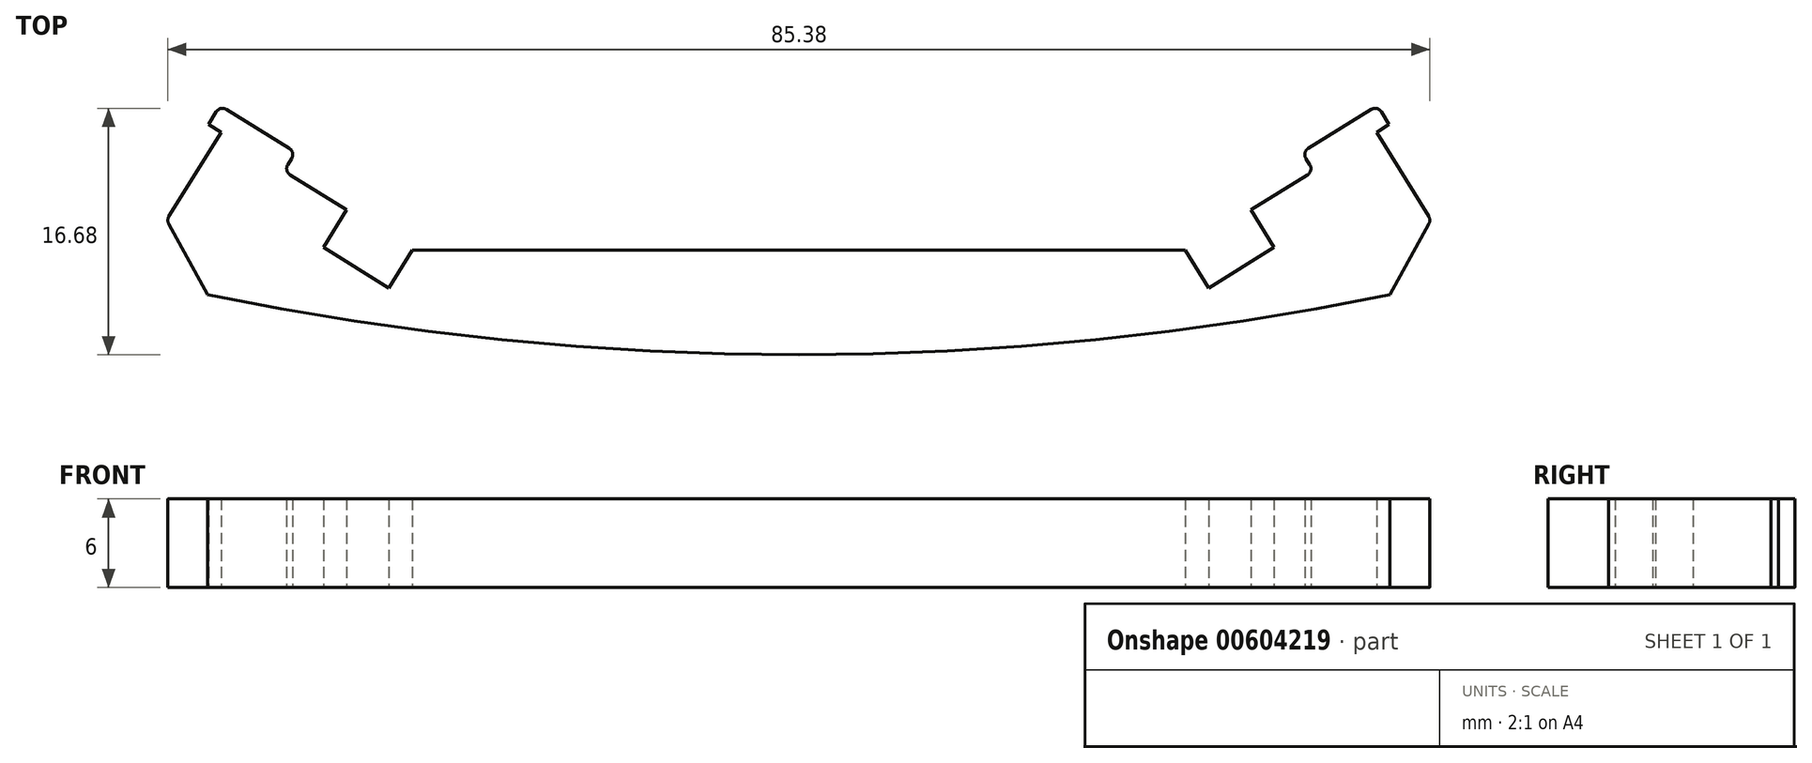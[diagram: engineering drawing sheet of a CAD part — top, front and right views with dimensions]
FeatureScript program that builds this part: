
annotation { "Feature Type Name" : "Feature", "Feature Type Description" : "" }
export const myFeature = defineFeature(function(context is Context, id is Id, definition is map)
    precondition{}
    {
        {
            var Q0;
            Q0=qCreatedBy(makeId("Top.planeOp"),FACE);
            var sketch = newSketch(context, id + "F0", { "sketchPlane" : qUnion([Q0])});
            skLineSegment(sketch, "E0", {"start": v(-40, 0) * mm, "end": v(40, 0) * mm, "construction": true});
            skLineSegment(sketch, "E1", {"start": v(-40, 0) * mm, "end": v(-70.77, 19.02) * mm, "construction": true});
            skLineSegment(sketch, "E2", {"start": v(-40, 0) * mm, "end": v(-26.49, 21.86) * mm, "construction": true});
            skLineSegment(sketch, "E3", {"start": v(-34.4, 8.1) * mm, "end": v(-30.58, 5.73) * mm});
            skLineSegment(sketch, "E4", {"start": v(-30.58, 5.73) * mm, "end": v(-32.16, 3.18) * mm});
            skLineSegment(sketch, "E5", {"start": v(-32.16, 3.18) * mm, "end": v(-27.73, 0.45) * mm});
            skLineSegment(sketch, "E6", {"start": v(-27.73, 0.45) * mm, "end": v(-26.16, 3) * mm});
            skLineSegment(sketch, "E7", {"start": v(0, 22.05) * mm, "end": v(0, -21.86) * mm, "construction": true});
            skLineSegment(sketch, "E8", {"start": v(-26.16, 3) * mm, "end": v(0, 3) * mm});
            skLineSegment(sketch, "E9", {"start": v(-39.08, 11) * mm, "end": v(-42.61, 5.28) * mm});
            skLineSegment(sketch, "E10.MirrorCS", {"start": v(27.73, 0.45) * mm, "end": v(26.16, 3) * mm});
            skLineSegment(sketch, "E11.MirrorCS", {"start": v(30.58, 5.73) * mm, "end": v(32.16, 3.18) * mm});
            skLineSegment(sketch, "E12.MirrorCS", {"start": v(39.08, 11) * mm, "end": v(42.61, 5.28) * mm});
            skLineSegment(sketch, "E13.MirrorCS", {"start": v(32.16, 3.18) * mm, "end": v(27.73, 0.45) * mm});
            skLineSegment(sketch, "E14.MirrorCS", {"start": v(34.4, 8.1) * mm, "end": v(30.58, 5.73) * mm});
            skLineSegment(sketch, "E15.MirrorCS", {"start": v(26.16, 3) * mm, "end": v(0, 3) * mm});
            skLineSegment(sketch, "E16", {"start": v(-39.08, 11) * mm, "end": v(-39.94, 11.52) * mm});
            skLineSegment(sketch, "E17", {"start": v(-39.94, 11.52) * mm, "end": v(-39.4, 12.37) * mm});
            skLineSegment(sketch, "E18", {"start": v(-38.72, 12.53) * mm, "end": v(-34.47, 9.9) * mm});
            skLineSegment(sketch, "E19", {"start": v(-34.3, 9.21) * mm, "end": v(-34.57, 8.79) * mm});
            skLineSegment(sketch, "E20.MirrorCS", {"start": v(39.08, 11) * mm, "end": v(39.94, 11.52) * mm});
            skLineSegment(sketch, "E21.MirrorCS", {"start": v(34.3, 9.21) * mm, "end": v(34.57, 8.79) * mm});
            skLineSegment(sketch, "E22.MirrorCS", {"start": v(38.72, 12.53) * mm, "end": v(34.47, 9.9) * mm});
            skLineSegment(sketch, "E23.MirrorCS", {"start": v(39.94, 11.52) * mm, "end": v(39.4, 12.37) * mm});
            skPoint(sketch, "E24.visualSharp", {"position": v(-39.15, 12.8) * mm});
            skArc(sketch, "E24.filletArc", {"start": v(-38.72, 12.53) * mm, "mid": v(-39.1, 12.6) * mm, "end": v(-39.4, 12.37) * mm});
            skPoint(sketch, "E25.visualSharp", {"position": v(-34.04, 9.64) * mm});
            skArc(sketch, "E25.filletArc", {"start": v(-34.3, 9.21) * mm, "mid": v(-34.24, 9.6) * mm, "end": v(-34.47, 9.9) * mm});
            skPoint(sketch, "E26.visualSharp", {"position": v(-34.83, 8.36) * mm});
            skArc(sketch, "E26.filletArc", {"start": v(-34.57, 8.79) * mm, "mid": v(-34.63, 8.41) * mm, "end": v(-34.4, 8.1) * mm});
            skPoint(sketch, "E27.visualSharp", {"position": v(34.83, 8.36) * mm});
            skArc(sketch, "E27.filletArc", {"start": v(34.4, 8.1) * mm, "mid": v(34.63, 8.41) * mm, "end": v(34.57, 8.79) * mm});
            skPoint(sketch, "E28.visualSharp", {"position": v(34.04, 9.64) * mm});
            skArc(sketch, "E28.filletArc", {"start": v(34.47, 9.9) * mm, "mid": v(34.24, 9.6) * mm, "end": v(34.3, 9.21) * mm});
            skPoint(sketch, "E29.visualSharp", {"position": v(39.15, 12.8) * mm});
            skArc(sketch, "E29.filletArc", {"start": v(39.4, 12.37) * mm, "mid": v(39.1, 12.6) * mm, "end": v(38.72, 12.53) * mm});
            skArc(sketch, "E30", {"start": v(-40, 0) * mm, "mid": v(0, -4.08) * mm, "end": v(40, 0) * mm});
            skLineSegment(sketch, "E31", {"start": v(-42.62, 4.78) * mm, "end": v(-40, 0) * mm});
            skLineSegment(sketch, "E32", {"start": v(40, 0) * mm, "end": v(42.62, 4.78) * mm});
            skPoint(sketch, "E33.visualSharp", {"position": v(42.77, 5.04) * mm});
            skArc(sketch, "E33.filletArc", {"start": v(42.62, 4.78) * mm, "mid": v(42.69, 5.03) * mm, "end": v(42.61, 5.28) * mm});
            skPoint(sketch, "E34.visualSharp", {"position": v(-42.77, 5.04) * mm});
            skArc(sketch, "E34.filletArc", {"start": v(-42.61, 5.28) * mm, "mid": v(-42.69, 5.03) * mm, "end": v(-42.62, 4.78) * mm});
            skSolve(sketch);
        }
        {
            var Q0;
            Q0 = qSketchRegion(id + "F0", true);
            extrude(context, id + "F1", {"entities" : qUnion([Q0]), "depth" : 6 * mm, "offsetDistance" : 25 * mm});
        }
    });
